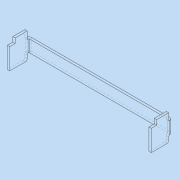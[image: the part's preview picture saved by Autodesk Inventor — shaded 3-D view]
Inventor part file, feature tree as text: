
AUTODESK INVENTOR PART (.ipt)
format: ipt  version: 2020 (Build 240168000, 168)  size: 186,880 bytes
history: native  units: mm
features: other x3, extrude x1
ambient origin geometry x8: Origin, YZ Plane, XZ Plane, XY Plane, X Axis, Y Axis, Z Axis, Center Point
bodies: Body1 (feature_tree)
feature tree (4):
  other  "實體1"
  extrude  "擠出1"  Depth=2.0mm TaperAngle=0.0deg
  other  "折彎零件1"
  other  "折彎零件2"
